FCSTD DOCUMENT  (FreeCAD 1.0R38641 +468 (Git))
Label: gridfinity-container-shapes
License: All rights reserved
LicenseURL: http://en.wikipedia.org/wiki/All_rights_reserved
objects: Sketcher::SketchObject×2, App::Part×2, PartDesign::CoordinateSystem×1
note: 5 computed .brp shape members not serialized (recipe doc carries the construction recipe); baked Part::Feature solids carry a one-line shape summary decoded from their .brp

FEATURE [PartDesign::CoordinateSystem] Local_CS_f824
  AttacherType = Attacher::AttachEngine3D
  MapMode = 2
FEATURE [Sketcher::SketchObject] PCB_Sketch_f824  label="gridfinity-1x1"
  ArcFitTolerance = 1e-06
  FullyConstrained = true
  MakeInternals = false
  sketch-geometry (10):
    g0: LineSegment StartX=-5.8e-15 StartY=-3.75 StartZ=0 EndX=-5.8e-15 EndY=-37.75 EndZ=0
    g1: LineSegment StartX=3.75 StartY=-41.5 StartZ=0 EndX=37.75 EndY=-41.5 EndZ=0
    g2: LineSegment StartX=41.5 StartY=-37.75 StartZ=0 EndX=41.5 EndY=-3.75 EndZ=0
    g3: LineSegment StartX=37.75 StartY=-1.8e-15 StartZ=0 EndX=3.75 EndY=-1.8e-15 EndZ=0
    g4: ArcOfCircle CenterX=3.75 CenterY=-3.75 CenterZ=0 NormalX=0 NormalY=0 NormalZ=1 AngleXU=0 Radius=3.75 StartAngle=1.5708 EndAngle=3.14159
    g5: ArcOfCircle CenterX=3.75 CenterY=-37.75 CenterZ=0 NormalX=0 NormalY=0 NormalZ=1 AngleXU=0 Radius=3.75 StartAngle=3.14159 EndAngle=4.71239
    g6: ArcOfCircle CenterX=37.75 CenterY=-37.75 CenterZ=0 NormalX=0 NormalY=0 NormalZ=1 AngleXU=0 Radius=3.75 StartAngle=4.71239 EndAngle=6.28319
    g7: ArcOfCircle CenterX=37.75 CenterY=-3.75 CenterZ=0 NormalX=0 NormalY=0 NormalZ=1 AngleXU=0 Radius=3.75 StartAngle=0 EndAngle=1.5708
    g8: GeomPoint [constr] X=-5.8e-15 Y=-1.8e-15 Z=0
    g9: GeomPoint [constr] X=41.5 Y=-41.5 Z=0
  constraints (23):
    c: Tangent(g0,g4) = -1.5708
    c: Tangent(g0,g5) = -1.5708
    c: Tangent(g1,g5) = -1.5708
    c: Tangent(g1,g6) = -1.5708
    c: Tangent(g2,g6) = -1.5708
    c: Tangent(g2,g7) = -1.5708
    c: Tangent(g3,g7) = -1.5708
    c: Tangent(g3,g4) = -1.5708
    c: Vertical(g0)
    c: Vertical(g2)
    c: Horizontal(g1)
    c: Horizontal(g3)
    c: Equal(g4,g5)
    c: Equal(g5,g6)
    c: Equal(g6,g7)
    c: PointOnObject(g8,g0)
    c: PointOnObject(g8,g3)
    c: PointOnObject(g9,g1)
    c: PointOnObject(g9,g2)
    c: Distance(g0,g2) = 41.5
    c: Distance(g1,g3) = 41.5
    c: Radius(g5) = 3.75
    c: Coincident(g8,g-1)
FEATURE [Sketcher::SketchObject] PCB_Sketch_f825  label="gridfinity-2x1"
  ArcFitTolerance = 1e-06
  FullyConstrained = true
  MakeInternals = false
  sketch-geometry (10):
    g0: LineSegment StartX=0 StartY=-3.75 StartZ=0 EndX=0 EndY=-37.75 EndZ=0
    g1: LineSegment StartX=3.75 StartY=-41.5 StartZ=0 EndX=79.75 EndY=-41.5 EndZ=0
    g2: LineSegment StartX=83.5 StartY=-37.75 StartZ=0 EndX=83.5 EndY=-3.75 EndZ=0
    g3: LineSegment StartX=79.75 StartY=-4.4e-15 StartZ=0 EndX=3.75 EndY=-4.4e-15 EndZ=0
    g4: ArcOfCircle CenterX=3.75 CenterY=-3.75 CenterZ=0 NormalX=0 NormalY=0 NormalZ=1 AngleXU=0 Radius=3.75 StartAngle=1.5708 EndAngle=3.14159
    g5: ArcOfCircle CenterX=3.75 CenterY=-37.75 CenterZ=0 NormalX=0 NormalY=0 NormalZ=1 AngleXU=0 Radius=3.75 StartAngle=3.14159 EndAngle=4.71239
    g6: ArcOfCircle CenterX=79.75 CenterY=-37.75 CenterZ=0 NormalX=0 NormalY=0 NormalZ=1 AngleXU=0 Radius=3.75 StartAngle=4.71239 EndAngle=6.28319
    g7: ArcOfCircle CenterX=79.75 CenterY=-3.75 CenterZ=0 NormalX=0 NormalY=0 NormalZ=1 AngleXU=0 Radius=3.75 StartAngle=0 EndAngle=1.5708
    g8: GeomPoint [constr] X=0 Y=0 Z=0
    g9: GeomPoint [constr] X=83.5 Y=-41.5 Z=0
  constraints (23):
    c: Tangent(g0,g4) = -1.5708
    c: Tangent(g0,g5) = -1.5708
    c: Tangent(g1,g5) = -1.5708
    c: Tangent(g1,g6) = -1.5708
    c: Tangent(g2,g6) = -1.5708
    c: Tangent(g2,g7) = -1.5708
    c: Tangent(g3,g7) = -1.5708
    c: Tangent(g3,g4) = -1.5708
    c: Vertical(g0)
    c: Vertical(g2)
    c: Horizontal(g1)
    c: Horizontal(g3)
    c: Equal(g4,g5)
    c: Equal(g5,g6)
    c: Equal(g6,g7)
    c: PointOnObject(g8,g0)
    c: PointOnObject(g8,g3)
    c: PointOnObject(g9,g1)
    c: PointOnObject(g9,g2)
    c: Distance(g0,g2) = 83.5
    c: Distance(g1,g3) = 41.5
    c: Radius(g5) = 3.75
    c: Coincident(g8,g-1)
FEATURE [App::Part] Board_Geoms_f824
  Group = -> [PCB_Sketch_f824,PCB_Sketch_f825]
  Origin = -> Origin
FEATURE [App::Part] Board_f824  label="gridfinity"
  Group = -> [Local_CS_f824,Board_Geoms_f824]
  Origin = -> Origin001
